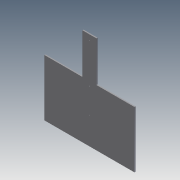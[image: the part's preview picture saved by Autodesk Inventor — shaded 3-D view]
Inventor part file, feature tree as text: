
AUTODESK INVENTOR PART (.ipt)
format: ipt  version: 2011 (Build 150239000, 239)  size: 1,086,976 bytes
history: native  units: in
note: dims shown in document units (in); Inventor stores cm internally (conversion verified against a paired STEP export)
features: extrude x36, sketch x36, fillet x1
ambient origin geometry x8: Origin, YZ Plane, XZ Plane, XY Plane, X Axis, Y Axis, Z Axis, Center Point
bodies: Solid1 (feature_tree)
feature tree (73):
  extrude  "Extrusion1"  Depth=35.0in
  extrude  "Extrusion2"  Depth=1.5in
  extrude  "Extrusion3"  Depth=0.75in
  extrude  "Extrusion4"  Depth=2.25in
  fillet  "Fillet1"  Radius=0.156in
  extrude  "Extrusion5"  Depth=0.25in TaperAngle=0.0deg
  extrude  "Extrusion6"  Depth=3.0in
  extrude  "Extrusion7"  Depth=1.0in
  extrude  "Extrusion8"  Depth=0.25in TaperAngle=0.0deg
  extrude  "Extrusion9"  Depth=3.5in
  extrude  "Extrusion10"  Depth=3.5in
  extrude  "Extrusion11"  Depth=0.25in TaperAngle=0.0deg
  extrude  "Extrusion12"  Depth=0.25in
  extrude  "Extrusion13"  Depth=1.0in
  extrude  "Extrusion14"  Depth=1.0in
  extrude  "Extrusion15"  Depth=1.0in
  extrude  "Extrusion16"  Depth=1.0in
  extrude  "Extrusion17"  Depth=1.0in
  extrude  "Extrusion18"  Depth=1.0in
  extrude  "Extrusion19"  Depth=1.0in
  extrude  "Extrusion20"  Depth=1.0in
  extrude  "Extrusion21"  Depth=1.0in
  extrude  "Extrusion22"  Depth=1.0in
  extrude  "Extrusion23"  Depth=2.0in
  extrude  "Extrusion24"  Depth=2.0in
  extrude  "Extrusion25"  Depth=2.0in
  extrude  "Extrusion26"  Depth=2.0in
  extrude  "Extrusion27"  Depth=2.0in
  extrude  "Extrusion28"  Depth=2.0in
  extrude  "Extrusion29"  Depth=2.0in
  extrude  "Extrusion30"  Depth=2.0in
  extrude  "Extrusion31"  Depth=2.0in
  extrude  "Extrusion32"  Depth=0.25in TaperAngle=0.0deg
  extrude  "Extrusion33"  Depth=0.75in
  extrude  "Extrusion34"  Depth=0.75in
  extrude  "Extrusion35"  Depth=2.0in
  extrude  "Extrusion36"  Depth=2.0in
  sketch  "Sketch1"  dims[d0=19.5in d1=35.0in]
  sketch  "Sketch2"  dims[d2=0.25in d3=0.0in d4=1.5in]
  sketch  "Sketch3"  dims[d5=3.0in d6=0.75in]
  sketch  "Sketch4"  dims[d7=0.75in d8=2.25in d9=0.156in]
  sketch  "Sketch5"  dims[d10=0.156in d11=0.25in d12=0.0in]
  sketch  "Sketch6"  dims[d13=1.5in d14=3.0in]
  sketch  "Sketch7"  dims[d15=1.5in d16=1.0in]
  sketch  "Sketch8"  dims[d17=32.25in d18=0.25in d19=0.0in]
  sketch  "Sketch9"  dims[d20=2.0in d21=3.5in]
  sketch  "Sketch10"  dims[d22=2.0in d23=3.5in]
  sketch  "Sketch11"  dims[d24=1.5in d25=0.25in d26=0.0in]
  sketch  "Sketch12"  dims[d27=0.25in d28=0.25in]
  sketch  "Sketch13"  dims[d29=0.25in d30=1.0in]
  sketch  "Sketch14"  dims[d31=1.0in d32=1.0in]
  sketch  "Sketch15"  dims[d33=1.0in d34=1.0in]
  sketch  "Sketch16"  dims[d35=1.0in d36=1.0in]
  sketch  "Sketch17"  dims[d37=1.0in d38=1.0in]
  sketch  "Sketch18"  dims[d39=1.0in d40=1.0in]
  sketch  "Sketch19"  dims[d41=1.0in d42=1.0in]
  sketch  "Sketch20"  dims[d43=1.0in d44=1.0in]
  sketch  "Sketch21"  dims[d45=1.0in d46=1.0in]
  sketch  "Sketch22"  dims[d47=1.0in d48=1.0in]
  sketch  "Sketch23"  dims[d49=0.25in d50=0.0in d51=2.0in]
  sketch  "Sketch24"  dims[d52=2.0in d53=2.0in]
  sketch  "Sketch25"  dims[d54=2.0in d55=2.0in]
  sketch  "Sketch26"  dims[d56=2.0in d57=2.0in]
  sketch  "Sketch27"  dims[d58=2.0in d59=2.0in]
  sketch  "Sketch28"  dims[d60=2.0in d61=2.0in]
  sketch  "Sketch29"  dims[d62=2.0in d63=2.0in]
  sketch  "Sketch30"  dims[d64=2.0in d65=2.0in]
  sketch  "Sketch31"  dims[d66=2.0in d67=2.0in]
  sketch  "Sketch32"  dims[d68=0.25in d69=0.0in d70=0.25in d71=0.0in]
  sketch  "Sketch33"  dims[d72=0.25in d73=0.0in d74=0.75in]
  sketch  "Sketch34"  dims[d75=0.25in d76=0.75in]
  sketch  "Sketch35"  dims[d77=0.25in d78=2.0in]
  sketch  "Sketch36"  dims[d79=2.0in d80=2.0in d81=2.0in d82=2.0in d83=2.0in d84=2.0in d85=2.0in d86=0.25in d87=0.0in d88=2.0in d89=2.0in d90=2.0in d91=2.0in d92=0.25in d93=0.0in d94=2.0in d95=2.0in d96=0.25in d97=0.0in d98=0.25in d99=0.25in d100=0.0in d101=9.0in d102=0.5in d103=0.75in d104=1.0in d105=0.0in d106=1.0in d107=0.0in d108=9.25in d109=0.25in d110=2.0in d111=0.25in d112=2.0in d113=4.0in d114=2.0in d115=1.0in d116=0.0in d117=0.25in d118=0.0in d119=0.25in d120=0.0in d121=0.5in d122=2.5in d123=0.5in d124=2.5in d125=0.156in d126=0.156in d127=0.25in d128=0.0in d129=0.25in d130=1.0in d131=0.0in d134=2.49in d135=8.0in d136=16.5in d137=0.185in d138=0.0925in d139=1.0in d140=0.0in d141=0.7in d142=1.0in d143=0.0in d144=1.0in d145=0.0in d146=0.25in d147=0.0in d148=0.25in d149=0.0in d150=5.853in d151=0.363in d152=0.363in d153=0.25in d154=0.0in d155=0.25in d156=0.0in d157=0.25in d158=0.0in d159=0.25in d160=0.0in d161=0.25in d162=0.0in d163=12.499in d164=1.0in d165=0.0in d166=1.5in d167=3.0in d168=8.5in d169=0.25in d170=0.0in d171=8.593in d172=0.25in d173=0.0in d174=0.25in d175=1.0in d176=0.0in d177=3.5in d178=0.25in d179=3.5in d180=0.25in d181=1.0in d182=0.0in d183=0.25in d184=0.0in d185=0.25in d186=0.0in]
